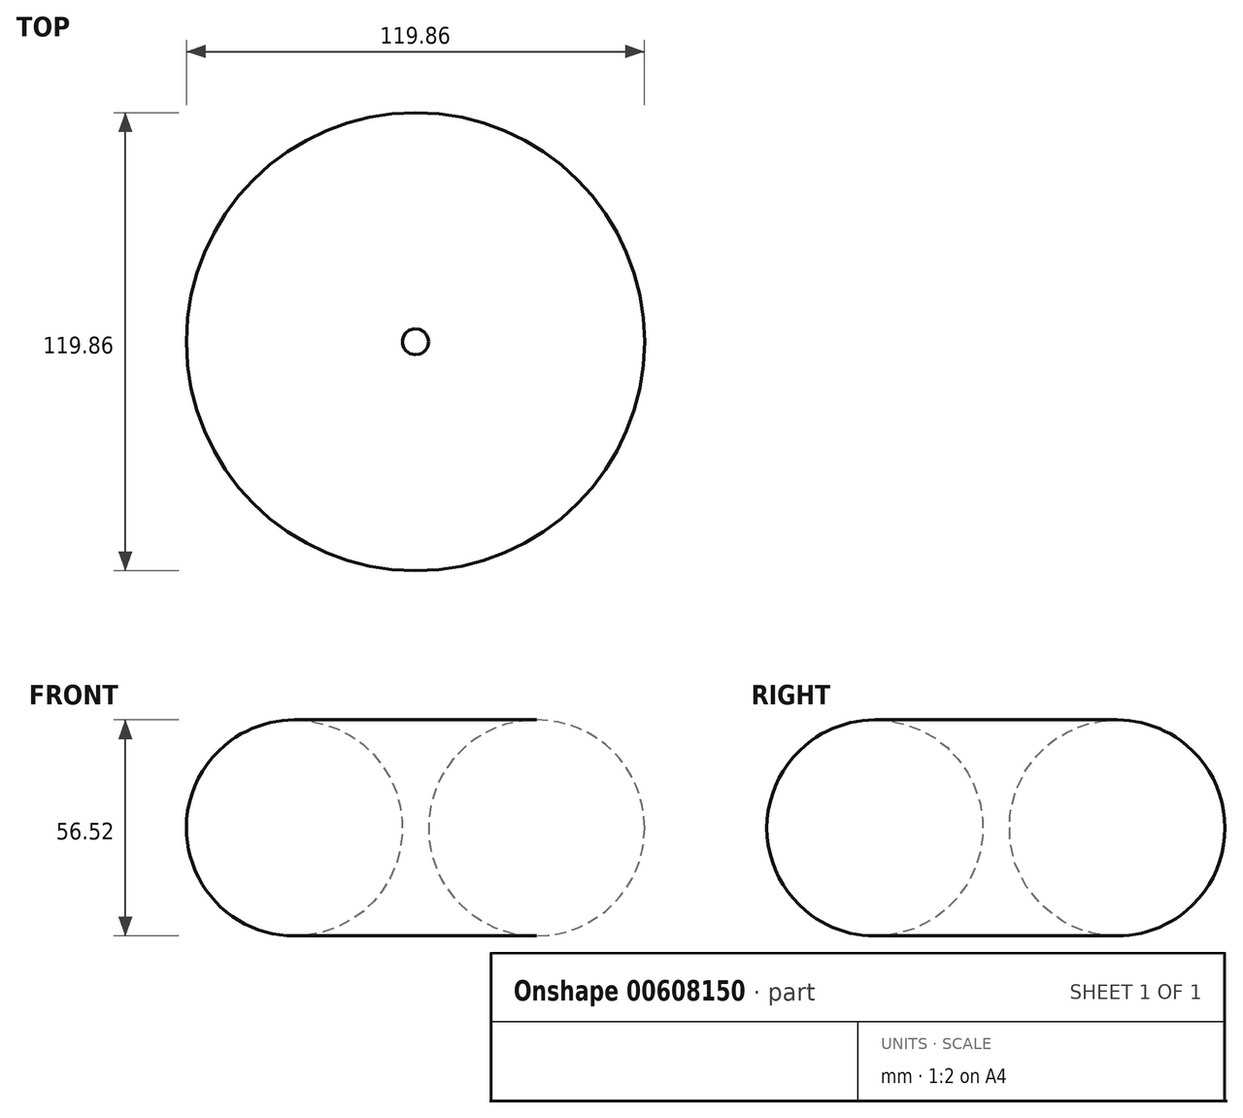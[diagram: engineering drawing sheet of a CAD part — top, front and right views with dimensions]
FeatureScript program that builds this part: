
annotation { "Feature Type Name" : "Feature", "Feature Type Description" : "" }
export const myFeature = defineFeature(function(context is Context, id is Id, definition is map)
    precondition{}
    {
        {
            var Q0;
            Q0=qCreatedBy(makeId("Front.planeOp"),FACE);
            var sketch = newSketch(context, id + "F0", { "sketchPlane" : qUnion([Q0])});
            skCircle(sketch, "E0", {"center": v(0, 0) * mm, "radius": 28.26 * mm});
            skLineSegment(sketch, "E1", {"start": v(31.67, 29.54) * mm, "end": v(31.67, -27.24) * mm});
            skSolve(sketch);
        }
        {
            var Q0;
            Q0 = qSketchRegion(id + "F0", true);
            var Q1;
            Q1=sQuery(id+"F0.wireOp",EDGE,"E1");
            revolve(context, id + "F1", {"entities" : qUnion([Q0]), "axis" : qUnion([Q1]), "revolveType" : RevolveType.FULL});
        }
    });
